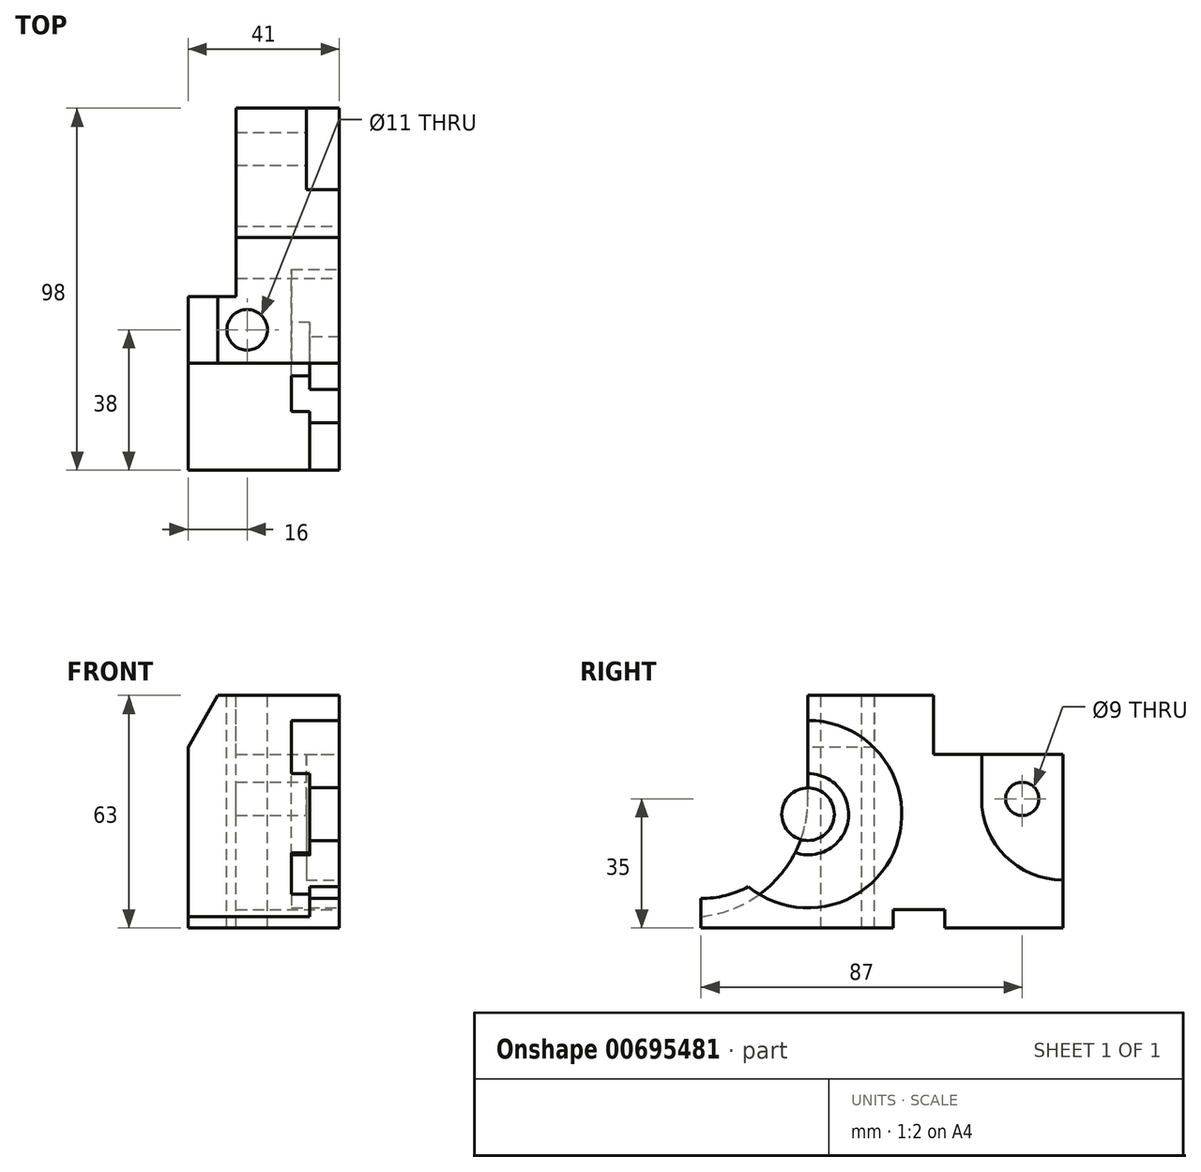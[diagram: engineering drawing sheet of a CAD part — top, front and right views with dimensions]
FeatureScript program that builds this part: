
annotation { "Feature Type Name" : "Feature", "Feature Type Description" : "" }
export const myFeature = defineFeature(function(context is Context, id is Id, definition is map)
    precondition{}
    {
        {
            var Q0;
            Q0=qCreatedBy(makeId("Top.planeOp"),FACE);
            var sketch = newSketch(context, id + "F0", { "sketchPlane" : qUnion([Q0])});
            skLineSegment(sketch, "E0.bottom", {"start": v(-20.5, 49) * mm, "end": v(20.5, 49) * mm});
            skLineSegment(sketch, "E0.top", {"start": v(-20.5, -49) * mm, "end": v(20.5, -49) * mm});
            skLineSegment(sketch, "E0.left", {"start": v(-20.5, 49) * mm, "end": v(-20.5, -49) * mm});
            skLineSegment(sketch, "E0.right", {"start": v(20.5, 49) * mm, "end": v(20.5, -49) * mm});
            skPoint(sketch, "E0.middle", {"position": v(0, 0) * mm});
            skSolve(sketch);
        }
        {
            var Q0;
            Q0=makeQuery(id+"F0.imprint","IMPRINT",FACE,{"disambiguationData":[TD([[makeQuery(id+"F0.imprint","IMPRINT",EDGE,{"derivedFrom":sQuery(id+"F0.wireOp",EDGE,"E0.bottom")}),-1.0]])]});
            extrude(context, id + "F1", {"entities" : qUnion([Q0]), "depth" : 63 * mm, "offsetDistance" : 25 * mm});
        }
        {
            var Q0;
            Q0=makeQuery(id+"F1.opExtrude","SWEPT_FACE",FACE,{"disambiguationData":[OSD([sQuery(id+"F0.wireOp",EDGE,"E0.right")])]});
            var sketch = newSketch(context, id + "F2", { "sketchPlane" : qUnion([Q0])});
            skPoint(sketch, "E1", {"position": v(49, 35) * mm});
            skArc(sketch, "E2", {"start": v(27, 35) * mm, "mid": v(33.44, 19.44) * mm, "end": v(49, 13) * mm});
            skLineSegment(sketch, "E3", {"start": v(27, 35) * mm, "end": v(27, 63) * mm});
            skLineSegment(sketch, "E4", {"start": v(27, 63) * mm, "end": v(49, 63) * mm});
            skLineSegment(sketch, "E5", {"start": v(49, 63) * mm, "end": v(49, 13) * mm});
            skPoint(sketch, "E6.orphan", {"position": v(71, 35) * mm});
            skSolve(sketch);
        }
        {
            var Q0;
            Q0=makeQuery(id+"F2.imprint","IMPRINT",FACE,{"disambiguationData":[TD([[makeQuery(id+"F2.imprint","IMPRINT",EDGE,{"derivedFrom":sQuery(id+"F2.wireOp",EDGE,"E2")}),1.0]])]});
            extrude(context, id + "F3", {"entities" : qUnion([Q0]), "operationType" : NewBodyOperationType.REMOVE, "oppositeDirection" : true, "depth" : 9 * mm, "offsetDistance" : 25 * mm});
        }
        {
            var Q0;
            Q0=makeQuery(id+"F1.opExtrude","CAP_FACE",FACE,{"disambiguationData":[OSD([sQuery(id+"F0.wireOp",EDGE,"E0.bottom"),sQuery(id+"F0.wireOp",EDGE,"E0.top"),sQuery(id+"F0.wireOp",EDGE,"E0.left"),sQuery(id+"F0.wireOp",EDGE,"E0.right")])],"isStart":false});
            var sketch = newSketch(context, id + "F4", { "sketchPlane" : qUnion([Q0])});
            skPoint(sketch, "E7.0", {"position": v(-20.5, 49) * mm});
            skLineSegment(sketch, "E8.bottom", {"start": v(-20.5, 49) * mm, "end": v(20.5, 49) * mm});
            skLineSegment(sketch, "E8.top", {"start": v(-20.5, 14) * mm, "end": v(20.5, 14) * mm});
            skLineSegment(sketch, "E8.left", {"start": v(-20.5, 49) * mm, "end": v(-20.5, 14) * mm});
            skLineSegment(sketch, "E8.right", {"start": v(20.5, 49) * mm, "end": v(20.5, 14) * mm});
            skSolve(sketch);
        }
        {
            var Q0;
            {var subQ4=sQuery(id+"F4.wireOp",EDGE,"E8.top");Q0=makeQuery(id+"F4.imprint","IMPRINT",FACE,{"disambiguationData":[TD([[makeQuery(id+"F4.imprint","IMPRINT",EDGE,{"derivedFrom":subQ4}),1.0]])]});}
            extrude(context, id + "F5", {"entities" : qUnion([Q0]), "operationType" : NewBodyOperationType.REMOVE, "oppositeDirection" : true, "depth" : 16 * mm, "offsetDistance" : 25 * mm});
        }
        {
            var Q0;
            Q0=makeQuery(id+"F1.opExtrude","SWEPT_FACE",FACE,{"disambiguationData":[OSD([sQuery(id+"F0.wireOp",EDGE,"E0.top")])]});
            var sketch = newSketch(context, id + "F6", { "sketchPlane" : qUnion([Q0])});
            skPoint(sketch, "E9.0", {"position": v(-20.5, 63) * mm});
            skLineSegment(sketch, "E10", {"start": v(-20.5, 49) * mm, "end": v(-12.42, 63) * mm});
            skLineSegment(sketch, "E11", {"start": v(-12.42, 63) * mm, "end": v(-20.5, 63) * mm});
            skLineSegment(sketch, "E12", {"start": v(-20.5, 49) * mm, "end": v(-20.5, 63) * mm});
            skSolve(sketch);
        }
        {
            var Q0;
            Q0=makeQuery(id+"F6.imprint","IMPRINT",FACE,{"disambiguationData":[TD([[makeQuery(id+"F6.imprint","IMPRINT",EDGE,{"derivedFrom":sQuery(id+"F6.wireOp",EDGE,"E10")}),1.0]])]});
            extrude(context, id + "F7", {"entities" : qUnion([Q0]), "operationType" : NewBodyOperationType.REMOVE, "endBound" : BoundingType.THROUGH_ALL, "oppositeDirection" : true, "depth" : 25 * mm, "offsetDistance" : 25 * mm});
        }
        {
            var Q0;
            Q0=makeQuery(id+"F1.opExtrude","CAP_FACE",FACE,{"disambiguationData":[OSD([sQuery(id+"F0.wireOp",EDGE,"E0.bottom"),sQuery(id+"F0.wireOp",EDGE,"E0.top"),sQuery(id+"F0.wireOp",EDGE,"E0.left"),sQuery(id+"F0.wireOp",EDGE,"E0.right")])],"isStart":false});
            cPlane(context, id + "F8", {"entities" : qUnion([Q0]), "cplaneType" : CPlaneType.OFFSET, "offset" : 0 * mm, "width" : 150 * mm, "height" : 150 * mm});
        }
        {
            var Q0;
            Q0=qCreatedBy(id+"F8.planeOp",FACE);
            var sketch = newSketch(context, id + "F9", { "sketchPlane" : qUnion([Q0])});
            skPoint(sketch, "E13.0", {"position": v(-20.5, 49) * mm});
            skPoint(sketch, "E14", {"position": v(-20.5, -2) * mm});
            skLineSegment(sketch, "E15.bottom", {"start": v(-20.5, -2) * mm, "end": v(-7.5, -2) * mm});
            skLineSegment(sketch, "E15.top", {"start": v(-20.5, 49) * mm, "end": v(-7.5, 49) * mm});
            skLineSegment(sketch, "E15.left", {"start": v(-20.5, -2) * mm, "end": v(-20.5, 49) * mm});
            skLineSegment(sketch, "E15.right", {"start": v(-7.5, -2) * mm, "end": v(-7.5, 49) * mm});
            skSolve(sketch);
        }
        {
            var Q0;
            Q0=makeQuery(id+"F9.imprint","IMPRINT",FACE,{"disambiguationData":[TD([[makeQuery(id+"F9.imprint","IMPRINT",EDGE,{"derivedFrom":sQuery(id+"F9.wireOp",EDGE,"E15.bottom")}),1.0]])]});
            extrude(context, id + "F10", {"entities" : qUnion([Q0]), "operationType" : NewBodyOperationType.REMOVE, "endBound" : BoundingType.THROUGH_ALL, "oppositeDirection" : true, "depth" : 25 * mm, "offsetDistance" : 25 * mm});
        }
        {
            var Q0;
            Q0=makeQuery(id+"F1.opExtrude","SWEPT_FACE",FACE,{"disambiguationData":[OSD([sQuery(id+"F0.wireOp",EDGE,"E0.right")])]});
            var sketch = newSketch(context, id + "F11", { "sketchPlane" : qUnion([Q0])});
            skPoint(sketch, "E16.0", {"position": v(49, 47) * mm});
            skCircle(sketch, "E17", {"center": v(-20, 30.83) * mm, "radius": 25.38 * mm});
            skSolve(sketch);
        }
        {
            var Q0;
            Q0=makeQuery(id+"F11.imprint","IMPRINT",FACE,{"disambiguationData":[TD([[makeQuery(id+"F11.imprint","IMPRINT",EDGE,{"derivedFrom":sQuery(id+"F11.wireOp",EDGE,"E17")}),1.0]])]});
            extrude(context, id + "F12", {"entities" : qUnion([Q0]), "operationType" : NewBodyOperationType.REMOVE, "oppositeDirection" : true, "depth" : 13 * mm, "offsetDistance" : 25 * mm});
        }
        {
            var Q0;
            Q0=makeQuery(id+"F12.boolean.opBoolean","COPY",FACE,{"derivedFrom":makeQuery(id+"F12.opExtrude","CAP_FACE",FACE,{"disambiguationData":[OSD([sQuery(id+"F11.wireOp",EDGE,"E17")])],"isStart":false})});
            var sketch = newSketch(context, id + "F13", { "sketchPlane" : qUnion([Q0])});
            skCircle(sketch, "E18", {"center": v(-20, 30.83) * mm, "radius": 11 * mm});
            skSolve(sketch);
        }
        {
            var Q0;
            Q0=makeQuery(id+"F13.imprint","IMPRINT",FACE,{"disambiguationData":[TD([[makeQuery(id+"F13.imprint","IMPRINT",EDGE,{"derivedFrom":sQuery(id+"F13.wireOp",EDGE,"E18")}),1.0]])]});
            extrude(context, id + "F14", {"entities" : qUnion([Q0]), "operationType" : NewBodyOperationType.ADD, "depth" : 5 * mm, "offsetDistance" : 25 * mm});
        }
        {
            var Q0;
            Q0=makeQuery(id+"F14.opExtrude","CAP_FACE",FACE,{"disambiguationData":[OSD([sQuery(id+"F13.wireOp",EDGE,"E18")])],"isStart":false});
            var sketch = newSketch(context, id + "F15", { "sketchPlane" : qUnion([Q0])});
            skCircle(sketch, "E19", {"center": v(-20, 30.83) * mm, "radius": 7.12 * mm});
            skSolve(sketch);
        }
        {
            var Q0;
            Q0=makeQuery(id+"F1.opExtrude","SWEPT_FACE",FACE,{"disambiguationData":[OSD([sQuery(id+"F0.wireOp",EDGE,"E0.left")])]});
            cPlane(context, id + "F16", {"entities" : qUnion([Q0]), "cplaneType" : CPlaneType.OFFSET, "offset" : 0 * mm, "width" : 150 * mm, "height" : 150 * mm});
        }
        {
            var Q0;
            Q0=qCreatedBy(id+"F16.planeOp",FACE);
            var sketch = newSketch(context, id + "F17", { "sketchPlane" : qUnion([Q0])});
            skPoint(sketch, "E20", {"position": v(52, 35) * mm});
            skArc(sketch, "E21", {"start": v(20, 35) * mm, "mid": v(68.25, 7.43) * mm, "end": v(67.5, 63) * mm});
            skLineSegment(sketch, "E22.0", {"start": v(2, 63) * mm, "end": v(49, 63) * mm, "construction": true});
            skLineSegment(sketch, "E23", {"start": v(20, 63) * mm, "end": v(20, 35) * mm});
            skLineSegment(sketch, "E24", {"start": v(20, 63) * mm, "end": v(67.5, 63) * mm});
            skSolve(sketch);
        }
        {
            var Q0;
            Q0=makeQuery(id+"F17.imprint","IMPRINT",FACE,{"disambiguationData":[TD([[makeQuery(id+"F17.imprint","IMPRINT",EDGE,{"derivedFrom":sQuery(id+"F17.wireOp",EDGE,"E21")}),1.0]])]});
            extrude(context, id + "F18", {"entities" : qUnion([Q0]), "operationType" : NewBodyOperationType.REMOVE, "endBound" : BoundingType.THROUGH_ALL, "oppositeDirection" : true, "depth" : 33 * mm, "offsetDistance" : 25 * mm});
        }
        {
            var Q0;
            Q0=makeQuery(id+"F15.imprint","IMPRINT",FACE,{"disambiguationData":[TD([[makeQuery(id+"F15.imprint","IMPRINT",EDGE,{"derivedFrom":sQuery(id+"F15.wireOp",EDGE,"E19")}),1.0]])]});
            extrude(context, id + "F19", {"entities" : qUnion([Q0]), "operationType" : NewBodyOperationType.ADD, "depth" : 8 * mm, "offsetDistance" : 25 * mm});
        }
        {
            var Q0;
            Q0=makeQuery(id+"F1.opExtrude","SWEPT_FACE",FACE,{"disambiguationData":[OSD([sQuery(id+"F0.wireOp",EDGE,"E0.right")])]});
            cPlane(context, id + "F20", {"entities" : qUnion([Q0]), "cplaneType" : CPlaneType.OFFSET, "offset" : 0 * mm, "width" : 150 * mm, "height" : 150 * mm});
        }
        {
            var Q0;
            Q0=qCreatedBy(id+"F20.planeOp",FACE);
            var sketch = newSketch(context, id + "F21", { "sketchPlane" : qUnion([Q0])});
            skPoint(sketch, "E25.0", {"position": v(-49, 0) * mm});
            skPoint(sketch, "E26", {"position": v(-49, 35) * mm});
            skArc(sketch, "E27", {"start": v(-49, 8) * mm, "mid": v(-42.37, 8.83) * mm, "end": v(-36.14, 11.26) * mm});
            skLineSegment(sketch, "E28", {"start": v(-49, 0) * mm, "end": v(-49, 8) * mm});
            skPoint(sketch, "E29.0", {"position": v(-33.16, 9.14) * mm});
            skPoint(sketch, "E30.0", {"position": v(-20, 30.83) * mm});
            skArc(sketch, "E31", {"start": v(-36.14, 11.26) * mm, "mid": v(-34.69, 10.14) * mm, "end": v(-33.16, 9.14) * mm});
            skLineSegment(sketch, "E32", {"start": v(-33.16, 9.14) * mm, "end": v(-33.16, 0) * mm});
            skLineSegment(sketch, "E33", {"start": v(-33.16, 0) * mm, "end": v(-49, 0) * mm});
            skSolve(sketch);
        }
        {
            var Q0;
            Q0=makeQuery(id+"F21.imprint","IMPRINT",FACE,{"disambiguationData":[TD([[makeQuery(id+"F21.imprint","IMPRINT",EDGE,{"derivedFrom":sQuery(id+"F21.wireOp",EDGE,"E27")}),-1.0]])]});
            extrude(context, id + "F22", {"entities" : qUnion([Q0]), "operationType" : NewBodyOperationType.ADD, "oppositeDirection" : true, "depth" : 8 * mm, "offsetDistance" : 25 * mm});
        }
        {
            var Q0;
            Q0=makeQuery(id+"F22.boolean.opBoolean","MERGE",FACE,{"derivedFrom":[makeQuery(id+"F1.opExtrude","SWEPT_FACE",FACE,{"disambiguationData":[OSD([sQuery(id+"F0.wireOp",EDGE,"E0.right")])]}),makeQuery(id+"F22.opExtrude","CAP_FACE",FACE,{"disambiguationData":[OSD([sQuery(id+"F21.wireOp",EDGE,"E27"),sQuery(id+"F21.wireOp",EDGE,"E28"),sQuery(id+"F21.wireOp",EDGE,"E31"),sQuery(id+"F21.wireOp",EDGE,"E32"),sQuery(id+"F21.wireOp",EDGE,"E33")])],"isStart":true})]});
            var sketch = newSketch(context, id + "F23", { "sketchPlane" : qUnion([Q0])});
            skLineSegment(sketch, "E34.bottom", {"start": v(17, 0) * mm, "end": v(3, 0) * mm});
            skLineSegment(sketch, "E34.top", {"start": v(17, 5) * mm, "end": v(3, 5) * mm});
            skLineSegment(sketch, "E34.left", {"start": v(17, 0) * mm, "end": v(17, 5) * mm});
            skLineSegment(sketch, "E34.right", {"start": v(3, 0) * mm, "end": v(3, 5) * mm});
            skSolve(sketch);
        }
        {
            var Q0;
            Q0=makeQuery(id+"F23.imprint","IMPRINT",FACE,{"disambiguationData":[TD([[makeQuery(id+"F23.imprint","IMPRINT",EDGE,{"derivedFrom":sQuery(id+"F23.wireOp",EDGE,"E34.bottom")}),-1.0]])]});
            extrude(context, id + "F24", {"entities" : qUnion([Q0]), "operationType" : NewBodyOperationType.REMOVE, "endBound" : BoundingType.THROUGH_ALL, "oppositeDirection" : true, "depth" : 25 * mm, "offsetDistance" : 25 * mm});
        }
        {
            var Q0;
            Q0=makeQuery(id+"F3.boolean.opBoolean","COPY",FACE,{"derivedFrom":makeQuery(id+"F3.opExtrude","CAP_FACE",FACE,{"disambiguationData":[OSD([sQuery(id+"F2.wireOp",EDGE,"E2"),sQuery(id+"F2.wireOp",EDGE,"E3"),sQuery(id+"F2.wireOp",EDGE,"E4"),sQuery(id+"F2.wireOp",EDGE,"E5")])],"isStart":false})});
            var sketch = newSketch(context, id + "F25", { "sketchPlane" : qUnion([Q0])});
            skCircle(sketch, "E35", {"center": v(38, 35) * mm, "radius": 4.5 * mm});
            skSolve(sketch);
        }
        {
            var Q0;
            Q0=makeQuery(id+"F25.imprint","IMPRINT",FACE,{"disambiguationData":[TD([[makeQuery(id+"F25.imprint","IMPRINT",EDGE,{"derivedFrom":sQuery(id+"F25.wireOp",EDGE,"E35")}),1.0]])]});
            extrude(context, id + "F26", {"entities" : qUnion([Q0]), "operationType" : NewBodyOperationType.REMOVE, "endBound" : BoundingType.THROUGH_ALL, "oppositeDirection" : true, "depth" : 25 * mm, "offsetDistance" : 25 * mm});
        }
        {
            var Q0;
            Q0=makeQuery(id+"F1.opExtrude","CAP_FACE",FACE,{"disambiguationData":[OSD([sQuery(id+"F0.wireOp",EDGE,"E0.bottom"),sQuery(id+"F0.wireOp",EDGE,"E0.top"),sQuery(id+"F0.wireOp",EDGE,"E0.left"),sQuery(id+"F0.wireOp",EDGE,"E0.right")])],"isStart":false});
            var sketch = newSketch(context, id + "F27", { "sketchPlane" : qUnion([Q0])});
            skCircle(sketch, "E36", {"center": v(-4.5, -11) * mm, "radius": 5.5 * mm});
            skSolve(sketch);
        }
        {
            var Q0;
            Q0=makeQuery(id+"F27.imprint","IMPRINT",FACE,{"disambiguationData":[TD([[makeQuery(id+"F27.imprint","IMPRINT",EDGE,{"derivedFrom":sQuery(id+"F27.wireOp",EDGE,"E36")}),1.0]])]});
            extrude(context, id + "F28", {"entities" : qUnion([Q0]), "operationType" : NewBodyOperationType.REMOVE, "endBound" : BoundingType.THROUGH_ALL, "oppositeDirection" : true, "depth" : 25 * mm, "offsetDistance" : 25 * mm});
        }
    });
